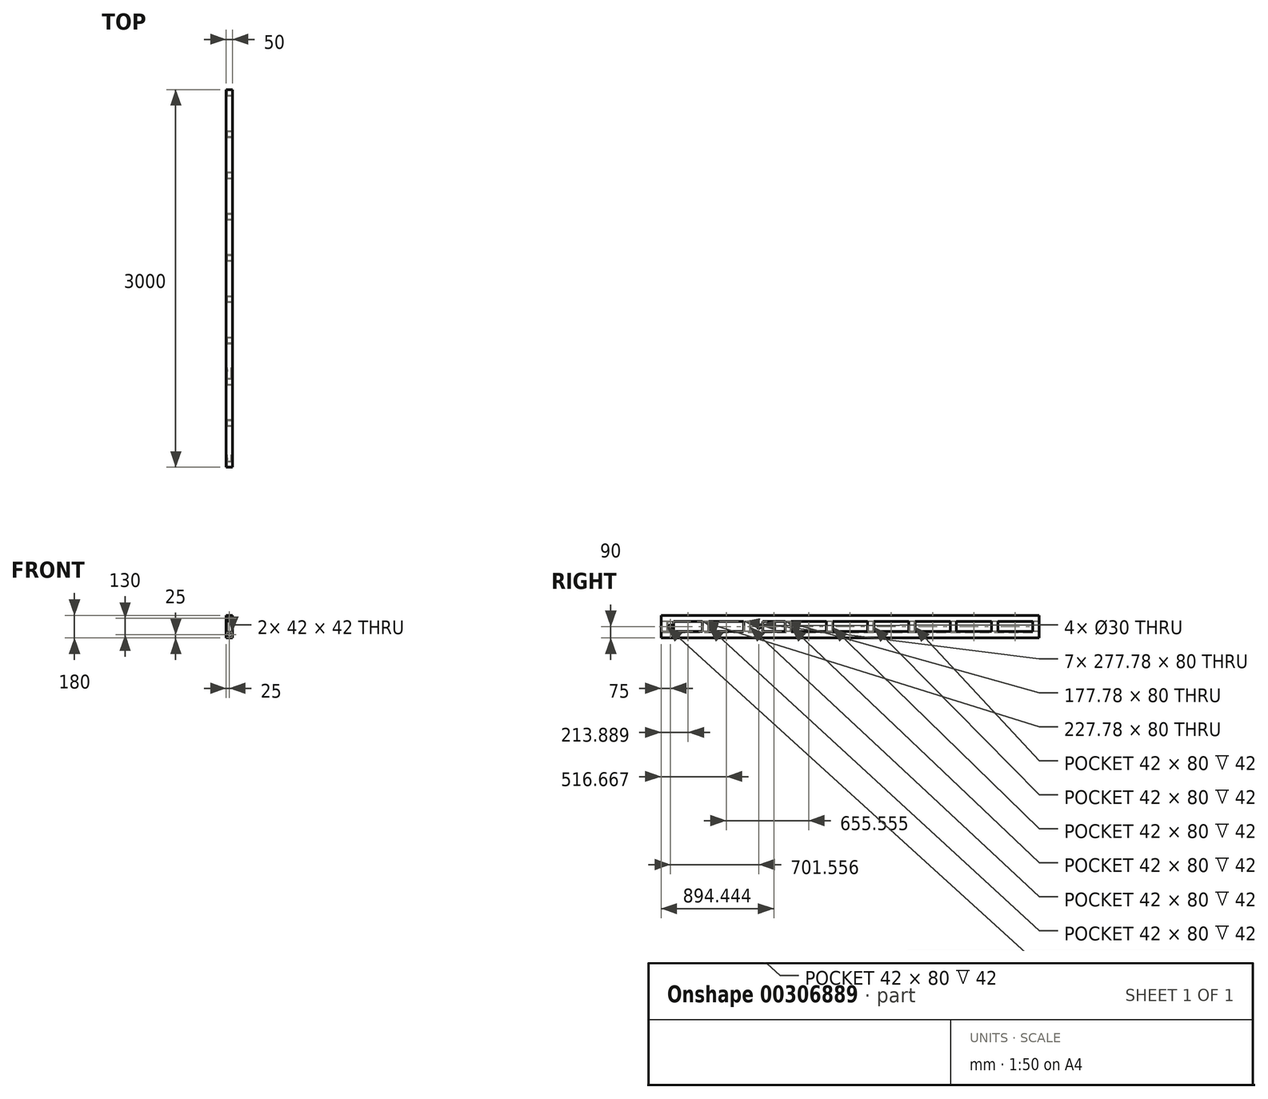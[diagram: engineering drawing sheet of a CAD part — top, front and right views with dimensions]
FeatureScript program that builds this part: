
annotation { "Feature Type Name" : "Feature", "Feature Type Description" : "" }
export const myFeature = defineFeature(function(context is Context, id is Id, definition is map)
    precondition{}
    {
        {
            var Q0;
            Q0=qCreatedBy(makeId("Front.planeOp"),FACE);
            var sketch = newSketch(context, id + "F0", { "sketchPlane" : qUnion([Q0])});
            skLineSegment(sketch, "E0.bottom", {"start": v(-25, 25) * mm, "end": v(25, 25) * mm});
            skLineSegment(sketch, "E0.top", {"start": v(-25, -25) * mm, "end": v(25, -25) * mm});
            skLineSegment(sketch, "E0.left", {"start": v(-25, 25) * mm, "end": v(-25, -25) * mm});
            skLineSegment(sketch, "E0.right", {"start": v(25, 25) * mm, "end": v(25, -25) * mm});
            skPoint(sketch, "E0.middle", {"position": v(0, 0) * mm});
            skLineSegment(sketch, "E1.0", {"start": v(-21, 21) * mm, "end": v(21, 21) * mm});
            skLineSegment(sketch, "E1.1", {"start": v(-21, 21) * mm, "end": v(-21, -21) * mm});
            skLineSegment(sketch, "E1.2", {"start": v(-21, -21) * mm, "end": v(21, -21) * mm});
            skLineSegment(sketch, "E1.3", {"start": v(21, 21) * mm, "end": v(21, -21) * mm});
            skPoint(sketch, "E2", {"position": v(-25, 25) * mm});
            skPoint(sketch, "E3", {"position": v(25, 25) * mm});
            skPoint(sketch, "E4", {"position": v(25, -25) * mm});
            skPoint(sketch, "E5", {"position": v(-25, -25) * mm});
            skLineSegment(sketch, "E6.bottom", {"start": v(-25, 155) * mm, "end": v(25, 155) * mm});
            skLineSegment(sketch, "E6.top", {"start": v(-25, 105) * mm, "end": v(25, 105) * mm});
            skLineSegment(sketch, "E6.left", {"start": v(-25, 155) * mm, "end": v(-25, 105) * mm});
            skLineSegment(sketch, "E6.right", {"start": v(25, 155) * mm, "end": v(25, 105) * mm});
            skPoint(sketch, "E6.middle", {"position": v(0, 130) * mm});
            skLineSegment(sketch, "E7.0", {"start": v(-21, 151) * mm, "end": v(21, 151) * mm});
            skLineSegment(sketch, "E7.1", {"start": v(-21, 151) * mm, "end": v(-21, 109) * mm});
            skLineSegment(sketch, "E7.2", {"start": v(-21, 109) * mm, "end": v(21, 109) * mm});
            skLineSegment(sketch, "E7.3", {"start": v(21, 151) * mm, "end": v(21, 109) * mm});
            skPoint(sketch, "E8", {"position": v(-25, 155) * mm});
            skPoint(sketch, "E9", {"position": v(25, 155) * mm});
            skPoint(sketch, "E10", {"position": v(25, 105) * mm});
            skPoint(sketch, "E11", {"position": v(-25, 105) * mm});
            skSolve(sketch);
        }
        {
            var Q0;
            Q0=makeQuery(id+"F0.imprint","IMPRINT",FACE,{"disambiguationData":[TD([[makeQuery(id+"F0.imprint","IMPRINT",EDGE,{"derivedFrom":sQuery(id+"F0.wireOp",EDGE,"E0.bottom")}),-1.0]])]});
            var Q1;
            Q1=makeQuery(id+"F0.imprint","IMPRINT",FACE,{"disambiguationData":[TD([[makeQuery(id+"F0.imprint","IMPRINT",EDGE,{"derivedFrom":sQuery(id+"F0.wireOp",EDGE,"E6.bottom")}),-1.0]])]});
            extrude(context, id + "F1", {"entities" : qUnion([Q0, Q1]), "depth" : 3000 * mm, "symmetric" : true});
        }
        {
            var Q0;
            Q0=makeQuery(id+"F1.opExtrude","SWEPT_FACE",FACE,{"disambiguationData":[OSD([sQuery(id+"F0.wireOp",EDGE,"E0.bottom")])]});
            var sketch = newSketch(context, id + "F2", { "sketchPlane" : qUnion([Q0])});
            skPoint(sketch, "E12", {"position": v(0, 1475) * mm});
            skPoint(sketch, "E13", {"position": v(-19.74, 1642.32) * mm});
            skPoint(sketch, "E14", {"position": v(-119.74, 1642.32) * mm});
            skPoint(sketch, "E15", {"position": v(180.26, 1642.32) * mm});
            skLineSegment(sketch, "E16.bottom", {"start": v(-25, 1500) * mm, "end": v(25, 1500) * mm});
            skLineSegment(sketch, "E16.top", {"start": v(-25, 1450) * mm, "end": v(25, 1450) * mm});
            skLineSegment(sketch, "E16.left", {"start": v(-25, 1500) * mm, "end": v(-25, 1450) * mm});
            skLineSegment(sketch, "E16.right", {"start": v(25, 1500) * mm, "end": v(25, 1450) * mm});
            skLineSegment(sketch, "E17.0", {"start": v(-21, 1496) * mm, "end": v(21, 1496) * mm});
            skLineSegment(sketch, "E17.1", {"start": v(-21, 1496) * mm, "end": v(-21, 1454) * mm});
            skLineSegment(sketch, "E17.2", {"start": v(-21, 1454) * mm, "end": v(21, 1454) * mm});
            skLineSegment(sketch, "E17.3", {"start": v(21, 1496) * mm, "end": v(21, 1454) * mm});
            skPoint(sketch, "E18", {"position": v(-25, 1500) * mm});
            skPoint(sketch, "E19", {"position": v(25, 1500) * mm});
            skPoint(sketch, "E20", {"position": v(25, 1450) * mm});
            skPoint(sketch, "E21", {"position": v(-25, 1450) * mm});
            skLineSegment(sketch, "E22.0.1.0", {"start": v(-25, 1172.22) * mm, "end": v(-25, 1122.22) * mm});
            skPoint(sketch, "E22.0.1.1", {"position": v(25, 1172.22) * mm});
            skLineSegment(sketch, "E22.0.1.2", {"start": v(25, 1172.22) * mm, "end": v(25, 1122.22) * mm});
            skPoint(sketch, "E22.0.1.3", {"position": v(-25, 1172.22) * mm});
            skLineSegment(sketch, "E22.0.1.4", {"start": v(-21, 1168.22) * mm, "end": v(-21, 1126.22) * mm});
            skLineSegment(sketch, "E22.0.1.5", {"start": v(-25, 1122.22) * mm, "end": v(25, 1122.22) * mm});
            skLineSegment(sketch, "E22.0.1.6", {"start": v(-21, 1168.22) * mm, "end": v(21, 1168.22) * mm});
            skLineSegment(sketch, "E22.0.1.7", {"start": v(21, 1168.22) * mm, "end": v(21, 1126.22) * mm});
            skLineSegment(sketch, "E22.0.1.8", {"start": v(-25, 1172.22) * mm, "end": v(25, 1172.22) * mm});
            skLineSegment(sketch, "E22.0.1.9", {"start": v(-21, 1126.22) * mm, "end": v(21, 1126.22) * mm});
            skPoint(sketch, "E22.0.1.10", {"position": v(0, 1147.22) * mm});
            skPoint(sketch, "E22.0.1.11", {"position": v(-25, 1122.22) * mm});
            skPoint(sketch, "E22.0.1.12", {"position": v(25, 1122.22) * mm});
            skPoint(sketch, "E22.0.1.13", {"position": v(0, 1147.22) * mm});
            skLineSegment(sketch, "E22.0.2.0", {"start": v(-25, 844.44) * mm, "end": v(-25, 794.44) * mm});
            skPoint(sketch, "E22.0.2.1", {"position": v(25, 844.44) * mm});
            skLineSegment(sketch, "E22.0.2.2", {"start": v(25, 844.44) * mm, "end": v(25, 794.44) * mm});
            skPoint(sketch, "E22.0.2.3", {"position": v(-25, 844.44) * mm});
            skLineSegment(sketch, "E22.0.2.4", {"start": v(-21, 840.44) * mm, "end": v(-21, 798.44) * mm});
            skLineSegment(sketch, "E22.0.2.5", {"start": v(-25, 794.44) * mm, "end": v(25, 794.44) * mm});
            skLineSegment(sketch, "E22.0.2.6", {"start": v(-21, 840.44) * mm, "end": v(21, 840.44) * mm});
            skLineSegment(sketch, "E22.0.2.7", {"start": v(21, 840.44) * mm, "end": v(21, 798.44) * mm});
            skLineSegment(sketch, "E22.0.2.8", {"start": v(-25, 844.44) * mm, "end": v(25, 844.44) * mm});
            skLineSegment(sketch, "E22.0.2.9", {"start": v(-21, 798.44) * mm, "end": v(21, 798.44) * mm});
            skPoint(sketch, "E22.0.2.10", {"position": v(0, 819.44) * mm});
            skPoint(sketch, "E22.0.2.11", {"position": v(-25, 794.44) * mm});
            skPoint(sketch, "E22.0.2.12", {"position": v(25, 794.44) * mm});
            skPoint(sketch, "E22.0.2.13", {"position": v(0, 819.44) * mm});
            skLineSegment(sketch, "E22.0.3.0", {"start": v(-25, 516.67) * mm, "end": v(-25, 466.67) * mm});
            skPoint(sketch, "E22.0.3.1", {"position": v(25, 516.67) * mm});
            skLineSegment(sketch, "E22.0.3.2", {"start": v(25, 516.67) * mm, "end": v(25, 466.67) * mm});
            skPoint(sketch, "E22.0.3.3", {"position": v(-25, 516.67) * mm});
            skLineSegment(sketch, "E22.0.3.4", {"start": v(-21, 512.67) * mm, "end": v(-21, 470.67) * mm});
            skLineSegment(sketch, "E22.0.3.5", {"start": v(-25, 466.67) * mm, "end": v(25, 466.67) * mm});
            skLineSegment(sketch, "E22.0.3.6", {"start": v(-21, 512.67) * mm, "end": v(21, 512.67) * mm});
            skLineSegment(sketch, "E22.0.3.7", {"start": v(21, 512.67) * mm, "end": v(21, 470.67) * mm});
            skLineSegment(sketch, "E22.0.3.8", {"start": v(-25, 516.67) * mm, "end": v(25, 516.67) * mm});
            skLineSegment(sketch, "E22.0.3.9", {"start": v(-21, 470.67) * mm, "end": v(21, 470.67) * mm});
            skPoint(sketch, "E22.0.3.10", {"position": v(0, 491.67) * mm});
            skPoint(sketch, "E22.0.3.11", {"position": v(-25, 466.67) * mm});
            skPoint(sketch, "E22.0.3.12", {"position": v(25, 466.67) * mm});
            skPoint(sketch, "E22.0.3.13", {"position": v(0, 491.67) * mm});
            skLineSegment(sketch, "E22.0.4.0", {"start": v(-25, 188.89) * mm, "end": v(-25, 138.89) * mm});
            skPoint(sketch, "E22.0.4.1", {"position": v(25, 188.89) * mm});
            skLineSegment(sketch, "E22.0.4.2", {"start": v(25, 188.89) * mm, "end": v(25, 138.89) * mm});
            skPoint(sketch, "E22.0.4.3", {"position": v(-25, 188.89) * mm});
            skLineSegment(sketch, "E22.0.4.4", {"start": v(-21, 184.89) * mm, "end": v(-21, 142.89) * mm});
            skLineSegment(sketch, "E22.0.4.5", {"start": v(-25, 138.89) * mm, "end": v(25, 138.89) * mm});
            skLineSegment(sketch, "E22.0.4.6", {"start": v(-21, 184.89) * mm, "end": v(21, 184.89) * mm});
            skLineSegment(sketch, "E22.0.4.7", {"start": v(21, 184.89) * mm, "end": v(21, 142.89) * mm});
            skLineSegment(sketch, "E22.0.4.8", {"start": v(-25, 188.89) * mm, "end": v(25, 188.89) * mm});
            skLineSegment(sketch, "E22.0.4.9", {"start": v(-21, 142.89) * mm, "end": v(21, 142.89) * mm});
            skPoint(sketch, "E22.0.4.10", {"position": v(0, 163.89) * mm});
            skPoint(sketch, "E22.0.4.11", {"position": v(-25, 138.89) * mm});
            skPoint(sketch, "E22.0.4.12", {"position": v(25, 138.89) * mm});
            skPoint(sketch, "E22.0.4.13", {"position": v(0, 163.89) * mm});
            skLineSegment(sketch, "E22.0.5.0", {"start": v(-25, -138.89) * mm, "end": v(-25, -188.89) * mm});
            skPoint(sketch, "E22.0.5.1", {"position": v(25, -138.89) * mm});
            skLineSegment(sketch, "E22.0.5.2", {"start": v(25, -138.89) * mm, "end": v(25, -188.89) * mm});
            skPoint(sketch, "E22.0.5.3", {"position": v(-25, -138.89) * mm});
            skLineSegment(sketch, "E22.0.5.4", {"start": v(-21, -142.89) * mm, "end": v(-21, -184.89) * mm});
            skLineSegment(sketch, "E22.0.5.5", {"start": v(-25, -188.89) * mm, "end": v(25, -188.89) * mm});
            skLineSegment(sketch, "E22.0.5.6", {"start": v(-21, -142.89) * mm, "end": v(21, -142.89) * mm});
            skLineSegment(sketch, "E22.0.5.7", {"start": v(21, -142.89) * mm, "end": v(21, -184.89) * mm});
            skLineSegment(sketch, "E22.0.5.8", {"start": v(-25, -138.89) * mm, "end": v(25, -138.89) * mm});
            skLineSegment(sketch, "E22.0.5.9", {"start": v(-21, -184.89) * mm, "end": v(21, -184.89) * mm});
            skPoint(sketch, "E22.0.5.10", {"position": v(0, -163.89) * mm});
            skPoint(sketch, "E22.0.5.11", {"position": v(-25, -188.89) * mm});
            skPoint(sketch, "E22.0.5.12", {"position": v(25, -188.89) * mm});
            skPoint(sketch, "E22.0.5.13", {"position": v(0, -163.89) * mm});
            skLineSegment(sketch, "E22.0.6.0", {"start": v(-25, -466.67) * mm, "end": v(-25, -516.67) * mm});
            skPoint(sketch, "E22.0.6.1", {"position": v(25, -466.67) * mm});
            skLineSegment(sketch, "E22.0.6.2", {"start": v(25, -466.67) * mm, "end": v(25, -516.67) * mm});
            skPoint(sketch, "E22.0.6.3", {"position": v(-25, -466.67) * mm});
            skLineSegment(sketch, "E22.0.6.4", {"start": v(-21, -470.67) * mm, "end": v(-21, -512.67) * mm});
            skLineSegment(sketch, "E22.0.6.5", {"start": v(-25, -516.67) * mm, "end": v(25, -516.67) * mm});
            skLineSegment(sketch, "E22.0.6.6", {"start": v(-21, -470.67) * mm, "end": v(21, -470.67) * mm});
            skLineSegment(sketch, "E22.0.6.7", {"start": v(21, -470.67) * mm, "end": v(21, -512.67) * mm});
            skLineSegment(sketch, "E22.0.6.8", {"start": v(-25, -466.67) * mm, "end": v(25, -466.67) * mm});
            skLineSegment(sketch, "E22.0.6.9", {"start": v(-21, -512.67) * mm, "end": v(21, -512.67) * mm});
            skPoint(sketch, "E22.0.6.10", {"position": v(0, -491.67) * mm});
            skPoint(sketch, "E22.0.6.11", {"position": v(-25, -516.67) * mm});
            skPoint(sketch, "E22.0.6.12", {"position": v(25, -516.67) * mm});
            skPoint(sketch, "E22.0.6.13", {"position": v(0, -491.67) * mm});
            skLineSegment(sketch, "E22.0.7.0", {"start": v(-25, -794.44) * mm, "end": v(-25, -844.44) * mm});
            skPoint(sketch, "E22.0.7.1", {"position": v(25, -794.44) * mm});
            skLineSegment(sketch, "E22.0.7.2", {"start": v(25, -794.44) * mm, "end": v(25, -844.44) * mm});
            skPoint(sketch, "E22.0.7.3", {"position": v(-25, -794.44) * mm});
            skLineSegment(sketch, "E22.0.7.4", {"start": v(-21, -798.44) * mm, "end": v(-21, -840.44) * mm});
            skLineSegment(sketch, "E22.0.7.5", {"start": v(-25, -844.44) * mm, "end": v(25, -844.44) * mm});
            skLineSegment(sketch, "E22.0.7.6", {"start": v(-21, -798.44) * mm, "end": v(21, -798.44) * mm});
            skLineSegment(sketch, "E22.0.7.7", {"start": v(21, -798.44) * mm, "end": v(21, -840.44) * mm});
            skLineSegment(sketch, "E22.0.7.8", {"start": v(-25, -794.44) * mm, "end": v(25, -794.44) * mm});
            skLineSegment(sketch, "E22.0.7.9", {"start": v(-21, -840.44) * mm, "end": v(21, -840.44) * mm});
            skPoint(sketch, "E22.0.7.10", {"position": v(0, -819.44) * mm});
            skPoint(sketch, "E22.0.7.11", {"position": v(-25, -844.44) * mm});
            skPoint(sketch, "E22.0.7.12", {"position": v(25, -844.44) * mm});
            skPoint(sketch, "E22.0.7.13", {"position": v(0, -819.44) * mm});
            skLineSegment(sketch, "E22.0.8.0", {"start": v(-25, -1122.22) * mm, "end": v(-25, -1172.22) * mm});
            skPoint(sketch, "E22.0.8.1", {"position": v(25, -1122.22) * mm});
            skLineSegment(sketch, "E22.0.8.2", {"start": v(25, -1122.22) * mm, "end": v(25, -1172.22) * mm});
            skPoint(sketch, "E22.0.8.3", {"position": v(-25, -1122.22) * mm});
            skLineSegment(sketch, "E22.0.8.4", {"start": v(-21, -1126.22) * mm, "end": v(-21, -1168.22) * mm});
            skLineSegment(sketch, "E22.0.8.5", {"start": v(-25, -1172.22) * mm, "end": v(25, -1172.22) * mm});
            skLineSegment(sketch, "E22.0.8.6", {"start": v(-21, -1126.22) * mm, "end": v(21, -1126.22) * mm});
            skLineSegment(sketch, "E22.0.8.7", {"start": v(21, -1126.22) * mm, "end": v(21, -1168.22) * mm});
            skLineSegment(sketch, "E22.0.8.8", {"start": v(-25, -1122.22) * mm, "end": v(25, -1122.22) * mm});
            skLineSegment(sketch, "E22.0.8.9", {"start": v(-21, -1168.22) * mm, "end": v(21, -1168.22) * mm});
            skPoint(sketch, "E22.0.8.10", {"position": v(0, -1147.22) * mm});
            skPoint(sketch, "E22.0.8.11", {"position": v(-25, -1172.22) * mm});
            skPoint(sketch, "E22.0.8.12", {"position": v(25, -1172.22) * mm});
            skPoint(sketch, "E22.0.8.13", {"position": v(0, -1147.22) * mm});
            skLineSegment(sketch, "E22.0.9.0", {"start": v(-25, -1450) * mm, "end": v(-25, -1500) * mm});
            skPoint(sketch, "E22.0.9.1", {"position": v(25, -1450) * mm});
            skLineSegment(sketch, "E22.0.9.2", {"start": v(25, -1450) * mm, "end": v(25, -1500) * mm});
            skPoint(sketch, "E22.0.9.3", {"position": v(-25, -1450) * mm});
            skLineSegment(sketch, "E22.0.9.4", {"start": v(-21, -1454) * mm, "end": v(-21, -1496) * mm});
            skLineSegment(sketch, "E22.0.9.5", {"start": v(-25, -1500) * mm, "end": v(25, -1500) * mm});
            skLineSegment(sketch, "E22.0.9.6", {"start": v(-21, -1454) * mm, "end": v(21, -1454) * mm});
            skLineSegment(sketch, "E22.0.9.7", {"start": v(21, -1454) * mm, "end": v(21, -1496) * mm});
            skLineSegment(sketch, "E22.0.9.8", {"start": v(-25, -1450) * mm, "end": v(25, -1450) * mm});
            skLineSegment(sketch, "E22.0.9.9", {"start": v(-21, -1496) * mm, "end": v(21, -1496) * mm});
            skPoint(sketch, "E22.0.9.10", {"position": v(0, -1475) * mm});
            skPoint(sketch, "E22.0.9.11", {"position": v(-25, -1500) * mm});
            skPoint(sketch, "E22.0.9.12", {"position": v(25, -1500) * mm});
            skPoint(sketch, "E22.0.9.13", {"position": v(0, -1475) * mm});
            skLineSegment(sketch, "E22.direction1", {"start": v(-25, 1450) * mm, "end": v(78, 1450) * mm, "construction": true});
            skLineSegment(sketch, "E22.direction2", {"start": v(-25, 1450) * mm, "end": v(-25, 1122.22) * mm, "construction": true});
            skSolve(sketch);
        }
        {
            var Q0;
            Q0 = qSketchRegion(id + "F2", true);
            extrude(context, id + "F3", {"entities" : qUnion([Q0]), "endBound" : BoundingType.UP_TO_NEXT, "depth" : 25 * mm});
        }
        {
            var Q0;
            Q0=makeQuery(id+"F1.opExtrude","SWEPT_BODY",BODY,{"disambiguationData":[OSD([sQuery(id+"F0.wireOp",EDGE,"E0.bottom"),sQuery(id+"F0.wireOp",EDGE,"E0.top"),sQuery(id+"F0.wireOp",EDGE,"E0.left"),sQuery(id+"F0.wireOp",EDGE,"E0.right"),sQuery(id+"F0.wireOp",EDGE,"E1.0"),sQuery(id+"F0.wireOp",EDGE,"E1.1"),sQuery(id+"F0.wireOp",EDGE,"E1.2"),sQuery(id+"F0.wireOp",EDGE,"E1.3")])]});
            var Q1;
            Q1=makeQuery(id+"F1.opExtrude","SWEPT_BODY",BODY,{"disambiguationData":[OSD([sQuery(id+"F0.wireOp",EDGE,"E6.bottom"),sQuery(id+"F0.wireOp",EDGE,"E6.top"),sQuery(id+"F0.wireOp",EDGE,"E6.left"),sQuery(id+"F0.wireOp",EDGE,"E6.right"),sQuery(id+"F0.wireOp",EDGE,"E7.0"),sQuery(id+"F0.wireOp",EDGE,"E7.1"),sQuery(id+"F0.wireOp",EDGE,"E7.2"),sQuery(id+"F0.wireOp",EDGE,"E7.3")])]});
            var Q2;
            Q2=makeQuery(id+"F3.opExtrude","SWEPT_BODY",BODY,{"disambiguationData":[OSD([sQuery(id+"F2.wireOp",EDGE,"E16.bottom"),sQuery(id+"F2.wireOp",EDGE,"E16.top"),sQuery(id+"F2.wireOp",EDGE,"E16.left"),sQuery(id+"F2.wireOp",EDGE,"E16.right"),sQuery(id+"F2.wireOp",EDGE,"E17.0"),sQuery(id+"F2.wireOp",EDGE,"E17.1"),sQuery(id+"F2.wireOp",EDGE,"E17.2"),sQuery(id+"F2.wireOp",EDGE,"E17.3")])]});
            var Q3;
            Q3=makeQuery(id+"F3.opExtrude","SWEPT_BODY",BODY,{"disambiguationData":[OSD([sQuery(id+"F2.wireOp",EDGE,"E22.0.1.0"),sQuery(id+"F2.wireOp",EDGE,"E22.0.1.2"),sQuery(id+"F2.wireOp",EDGE,"E22.0.1.4"),sQuery(id+"F2.wireOp",EDGE,"E22.0.1.5"),sQuery(id+"F2.wireOp",EDGE,"E22.0.1.6"),sQuery(id+"F2.wireOp",EDGE,"E22.0.1.7"),sQuery(id+"F2.wireOp",EDGE,"E22.0.1.8"),sQuery(id+"F2.wireOp",EDGE,"E22.0.1.9")])]});
            var Q4;
            Q4=makeQuery(id+"F3.opExtrude","SWEPT_BODY",BODY,{"disambiguationData":[OSD([sQuery(id+"F2.wireOp",EDGE,"E22.0.2.0"),sQuery(id+"F2.wireOp",EDGE,"E22.0.2.2"),sQuery(id+"F2.wireOp",EDGE,"E22.0.2.4"),sQuery(id+"F2.wireOp",EDGE,"E22.0.2.5"),sQuery(id+"F2.wireOp",EDGE,"E22.0.2.6"),sQuery(id+"F2.wireOp",EDGE,"E22.0.2.7"),sQuery(id+"F2.wireOp",EDGE,"E22.0.2.8"),sQuery(id+"F2.wireOp",EDGE,"E22.0.2.9")])]});
            var Q5;
            Q5=makeQuery(id+"F3.opExtrude","SWEPT_BODY",BODY,{"disambiguationData":[OSD([sQuery(id+"F2.wireOp",EDGE,"E22.0.3.0"),sQuery(id+"F2.wireOp",EDGE,"E22.0.3.2"),sQuery(id+"F2.wireOp",EDGE,"E22.0.3.4"),sQuery(id+"F2.wireOp",EDGE,"E22.0.3.5"),sQuery(id+"F2.wireOp",EDGE,"E22.0.3.6"),sQuery(id+"F2.wireOp",EDGE,"E22.0.3.7"),sQuery(id+"F2.wireOp",EDGE,"E22.0.3.8"),sQuery(id+"F2.wireOp",EDGE,"E22.0.3.9")])]});
            var Q6;
            Q6=makeQuery(id+"F3.opExtrude","SWEPT_BODY",BODY,{"disambiguationData":[OSD([sQuery(id+"F2.wireOp",EDGE,"E22.0.4.0"),sQuery(id+"F2.wireOp",EDGE,"E22.0.4.2"),sQuery(id+"F2.wireOp",EDGE,"E22.0.4.4"),sQuery(id+"F2.wireOp",EDGE,"E22.0.4.5"),sQuery(id+"F2.wireOp",EDGE,"E22.0.4.6"),sQuery(id+"F2.wireOp",EDGE,"E22.0.4.7"),sQuery(id+"F2.wireOp",EDGE,"E22.0.4.8"),sQuery(id+"F2.wireOp",EDGE,"E22.0.4.9")])]});
            var Q7;
            Q7=makeQuery(id+"F3.opExtrude","SWEPT_BODY",BODY,{"disambiguationData":[OSD([sQuery(id+"F2.wireOp",EDGE,"E22.0.5.0"),sQuery(id+"F2.wireOp",EDGE,"E22.0.5.2"),sQuery(id+"F2.wireOp",EDGE,"E22.0.5.4"),sQuery(id+"F2.wireOp",EDGE,"E22.0.5.5"),sQuery(id+"F2.wireOp",EDGE,"E22.0.5.6"),sQuery(id+"F2.wireOp",EDGE,"E22.0.5.7"),sQuery(id+"F2.wireOp",EDGE,"E22.0.5.8"),sQuery(id+"F2.wireOp",EDGE,"E22.0.5.9")])]});
            var Q8;
            Q8=makeQuery(id+"F3.opExtrude","SWEPT_BODY",BODY,{"disambiguationData":[OSD([sQuery(id+"F2.wireOp",EDGE,"E22.0.6.0"),sQuery(id+"F2.wireOp",EDGE,"E22.0.6.2"),sQuery(id+"F2.wireOp",EDGE,"E22.0.6.4"),sQuery(id+"F2.wireOp",EDGE,"E22.0.6.5"),sQuery(id+"F2.wireOp",EDGE,"E22.0.6.6"),sQuery(id+"F2.wireOp",EDGE,"E22.0.6.7"),sQuery(id+"F2.wireOp",EDGE,"E22.0.6.8"),sQuery(id+"F2.wireOp",EDGE,"E22.0.6.9")])]});
            var Q9;
            Q9=makeQuery(id+"F3.opExtrude","SWEPT_BODY",BODY,{"disambiguationData":[OSD([sQuery(id+"F2.wireOp",EDGE,"E22.0.7.0"),sQuery(id+"F2.wireOp",EDGE,"E22.0.7.2"),sQuery(id+"F2.wireOp",EDGE,"E22.0.7.4"),sQuery(id+"F2.wireOp",EDGE,"E22.0.7.5"),sQuery(id+"F2.wireOp",EDGE,"E22.0.7.6"),sQuery(id+"F2.wireOp",EDGE,"E22.0.7.7"),sQuery(id+"F2.wireOp",EDGE,"E22.0.7.8"),sQuery(id+"F2.wireOp",EDGE,"E22.0.7.9")])]});
            var Q10;
            Q10=makeQuery(id+"F3.opExtrude","SWEPT_BODY",BODY,{"disambiguationData":[OSD([sQuery(id+"F2.wireOp",EDGE,"E22.0.8.0"),sQuery(id+"F2.wireOp",EDGE,"E22.0.8.2"),sQuery(id+"F2.wireOp",EDGE,"E22.0.8.4"),sQuery(id+"F2.wireOp",EDGE,"E22.0.8.5"),sQuery(id+"F2.wireOp",EDGE,"E22.0.8.6"),sQuery(id+"F2.wireOp",EDGE,"E22.0.8.7"),sQuery(id+"F2.wireOp",EDGE,"E22.0.8.8"),sQuery(id+"F2.wireOp",EDGE,"E22.0.8.9")])]});
            var Q11;
            Q11=makeQuery(id+"F3.opExtrude","SWEPT_BODY",BODY,{"disambiguationData":[OSD([sQuery(id+"F2.wireOp",EDGE,"E22.0.9.0"),sQuery(id+"F2.wireOp",EDGE,"E22.0.9.2"),sQuery(id+"F2.wireOp",EDGE,"E22.0.9.4"),sQuery(id+"F2.wireOp",EDGE,"E22.0.9.5"),sQuery(id+"F2.wireOp",EDGE,"E22.0.9.6"),sQuery(id+"F2.wireOp",EDGE,"E22.0.9.7"),sQuery(id+"F2.wireOp",EDGE,"E22.0.9.8"),sQuery(id+"F2.wireOp",EDGE,"E22.0.9.9")])]});
            booleanBodies(context, id + "F4", {"operationType" : BooleanOperationType.UNION, "tools" : qUnion([Q0, Q1, Q2, Q3, Q4, Q5, Q6, Q7, Q8, Q9, Q10, Q11])});
        }
        {
            var Q0;
            Q0=makeQuery(id+"F4.opBoolean","SPLIT",FACE,{"disambiguationData":[TD([makeQuery(id+"F3.opExtrude","SWEPT_FACE",FACE,{"disambiguationData":[OSD([sQuery(id+"F2.wireOp",EDGE,"E22.0.8.5")])]})])],"derivedFrom":makeQuery(id+"F1.opExtrude","SWEPT_FACE",FACE,{"disambiguationData":[OSD([sQuery(id+"F0.wireOp",EDGE,"E0.bottom")])]})});
            var sketch = newSketch(context, id + "F5", { "sketchPlane" : qUnion([Q0])});
            skPoint(sketch, "E23.0", {"position": v(25, -1450) * mm});
            skPoint(sketch, "E24.0", {"position": v(25, -794.44) * mm});
            skLineSegment(sketch, "E25.bottom", {"start": v(25, -1450) * mm, "end": v(15, -1450) * mm});
            skLineSegment(sketch, "E25.top", {"start": v(25, -1400) * mm, "end": v(15, -1400) * mm});
            skLineSegment(sketch, "E25.left", {"start": v(25, -1450) * mm, "end": v(25, -1400) * mm});
            skLineSegment(sketch, "E25.right", {"start": v(15, -1450) * mm, "end": v(15, -1400) * mm});
            skLineSegment(sketch, "E26.bottom", {"start": v(25, -794.44) * mm, "end": v(15, -794.44) * mm});
            skLineSegment(sketch, "E26.top", {"start": v(25, -694.44) * mm, "end": v(15, -694.44) * mm});
            skLineSegment(sketch, "E26.left", {"start": v(25, -794.44) * mm, "end": v(25, -694.44) * mm});
            skLineSegment(sketch, "E26.right", {"start": v(15, -794.44) * mm, "end": v(15, -694.44) * mm});
            skLineSegment(sketch, "E27.MirrorCS", {"start": v(-25, -1450) * mm, "end": v(-15, -1450) * mm});
            skLineSegment(sketch, "E28.MirrorCS", {"start": v(-15, -1450) * mm, "end": v(-15, -1400) * mm});
            skLineSegment(sketch, "E29.MirrorCS", {"start": v(-25, -1450) * mm, "end": v(-25, -1400) * mm});
            skLineSegment(sketch, "E30.MirrorCS", {"start": v(-25, -1400) * mm, "end": v(-15, -1400) * mm});
            skLineSegment(sketch, "E31.MirrorCS", {"start": v(-25, -694.44) * mm, "end": v(-15, -694.44) * mm});
            skLineSegment(sketch, "E32.MirrorCS", {"start": v(-15, -794.44) * mm, "end": v(-15, -694.44) * mm});
            skLineSegment(sketch, "E33.MirrorCS", {"start": v(-25, -794.44) * mm, "end": v(-15, -794.44) * mm});
            skLineSegment(sketch, "E34.MirrorCS", {"start": v(-25, -794.44) * mm, "end": v(-25, -694.44) * mm});
            skSolve(sketch);
        }
        {
            var Q0;
            Q0 = qSketchRegion(id + "F5", true);
            extrude(context, id + "F6", {"entities" : qUnion([Q0]), "operationType" : NewBodyOperationType.ADD, "endBound" : BoundingType.UP_TO_NEXT, "depth" : 25 * mm});
        }
        {
            var Q0;
            Q0=makeQuery(id+"F6.boolean.opBoolean","MERGE",FACE,{"derivedFrom":[makeQuery(id+"F4.opBoolean","MERGE",FACE,{"derivedFrom":[makeQuery(id+"F1.opExtrude","SWEPT_FACE",FACE,{"disambiguationData":[OSD([sQuery(id+"F0.wireOp",EDGE,"E0.right")])]}),makeQuery(id+"F1.opExtrude","SWEPT_FACE",FACE,{"disambiguationData":[OSD([sQuery(id+"F0.wireOp",EDGE,"E6.right")])]}),makeQuery(id+"F3.opExtrude","SWEPT_FACE",FACE,{"disambiguationData":[OSD([sQuery(id+"F2.wireOp",EDGE,"E16.right")])]}),makeQuery(id+"F3.opExtrude","SWEPT_FACE",FACE,{"disambiguationData":[OSD([sQuery(id+"F2.wireOp",EDGE,"E22.0.1.2")])]}),makeQuery(id+"F3.opExtrude","SWEPT_FACE",FACE,{"disambiguationData":[OSD([sQuery(id+"F2.wireOp",EDGE,"E22.0.2.2")])]}),makeQuery(id+"F3.opExtrude","SWEPT_FACE",FACE,{"disambiguationData":[OSD([sQuery(id+"F2.wireOp",EDGE,"E22.0.3.2")])]}),makeQuery(id+"F3.opExtrude","SWEPT_FACE",FACE,{"disambiguationData":[OSD([sQuery(id+"F2.wireOp",EDGE,"E22.0.4.2")])]}),makeQuery(id+"F3.opExtrude","SWEPT_FACE",FACE,{"disambiguationData":[OSD([sQuery(id+"F2.wireOp",EDGE,"E22.0.5.2")])]}),makeQuery(id+"F3.opExtrude","SWEPT_FACE",FACE,{"disambiguationData":[OSD([sQuery(id+"F2.wireOp",EDGE,"E22.0.6.2")])]}),makeQuery(id+"F3.opExtrude","SWEPT_FACE",FACE,{"disambiguationData":[OSD([sQuery(id+"F2.wireOp",EDGE,"E22.0.7.2")])]}),makeQuery(id+"F3.opExtrude","SWEPT_FACE",FACE,{"disambiguationData":[OSD([sQuery(id+"F2.wireOp",EDGE,"E22.0.8.2")])]}),makeQuery(id+"F3.opExtrude","SWEPT_FACE",FACE,{"disambiguationData":[OSD([sQuery(id+"F2.wireOp",EDGE,"E22.0.9.2")])]})]}),makeQuery(id+"F6.opExtrude","SWEPT_FACE",FACE,{"disambiguationData":[OSD([sQuery(id+"F5.wireOp",EDGE,"E25.left")])]}),makeQuery(id+"F6.opExtrude","SWEPT_FACE",FACE,{"disambiguationData":[OSD([sQuery(id+"F5.wireOp",EDGE,"E26.left")])]})]});
            var sketch = newSketch(context, id + "F7", { "sketchPlane" : qUnion([Q0])});
            skPoint(sketch, "E35.0", {"position": v(-1400, 25) * mm});
            skPoint(sketch, "E36.0", {"position": v(-694.44, 25) * mm});
            skPoint(sketch, "E37", {"position": v(-723.44, 65) * mm});
            skPoint(sketch, "E38", {"position": v(-1425, 65) * mm});
            skCircle(sketch, "E39", {"center": v(-723.44, 65) * mm, "radius": 15 * mm});
            skCircle(sketch, "E40", {"center": v(-1425, 65) * mm, "radius": 15 * mm});
            skSolve(sketch);
        }
        {
            var Q0;
            Q0 = qSketchRegion(id + "F7", true);
            extrude(context, id + "F8", {"entities" : qUnion([Q0]), "operationType" : NewBodyOperationType.REMOVE, "endBound" : BoundingType.THROUGH_ALL, "oppositeDirection" : true, "depth" : 25 * mm});
        }
    });
